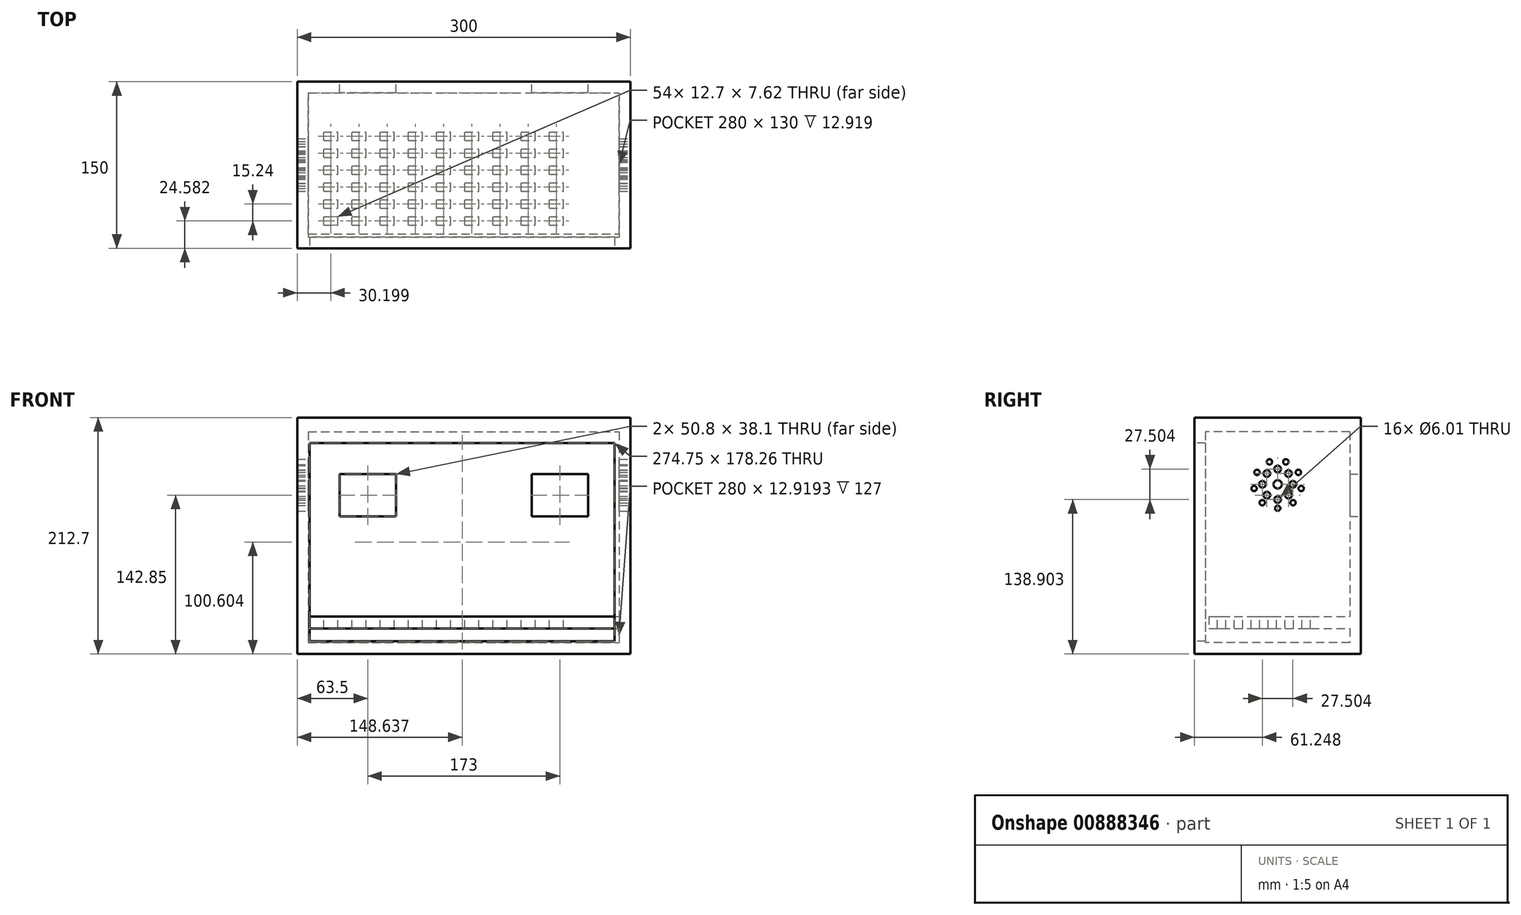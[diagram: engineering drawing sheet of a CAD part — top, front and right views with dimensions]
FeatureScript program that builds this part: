
annotation { "Feature Type Name" : "Feature", "Feature Type Description" : "" }
export const myFeature = defineFeature(function(context is Context, id is Id, definition is map)
    precondition{}
    {
        {
            var Q0;
            Q0=qCreatedBy(makeId("Top.planeOp"),FACE);
            var sketch = newSketch(context, id + "F0", { "sketchPlane" : qUnion([Q0])});
            skLineSegment(sketch, "E0.bottom", {"start": v(-150, 75) * mm, "end": v(150, 75) * mm});
            skLineSegment(sketch, "E0.top", {"start": v(-150, -75) * mm, "end": v(150, -75) * mm});
            skLineSegment(sketch, "E0.left", {"start": v(-150, 75) * mm, "end": v(-150, -75) * mm});
            skLineSegment(sketch, "E0.right", {"start": v(150, 75) * mm, "end": v(150, -75) * mm});
            skSolve(sketch);
        }
        {
            var Q0;
            Q0 = qSketchRegion(id + "F0", true);
            extrude(context, id + "F1", {"entities" : qUnion([Q0]), "depth" : 200 * mm, "offsetDistance" : 25.4 * mm});
        }
        {
            var Q0;
            Q0=makeQuery(id+"F1.opExtrude","CAP_FACE",FACE,{"disambiguationData":[OSD([sQuery(id+"F0.wireOp",EDGE,"E0.bottom"),sQuery(id+"F0.wireOp",EDGE,"E0.top"),sQuery(id+"F0.wireOp",EDGE,"E0.left"),sQuery(id+"F0.wireOp",EDGE,"E0.right")])],"isStart":false});
            shell(context, id + "F2", {"entities" : qUnion([Q0]), "thickness" : 10 * mm});
        }
        {
            var Q0;
            Q0=makeQuery(id+"F1.opExtrude","SWEPT_FACE",FACE,{"disambiguationData":[OSD([sQuery(id+"F0.wireOp",EDGE,"E0.top")])]});
            var sketch = newSketch(context, id + "F3", { "sketchPlane" : qUnion([Q0])});
            skLineSegment(sketch, "E1.bottom", {"start": v(-138.74, 11.48) * mm, "end": v(136.01, 11.48) * mm});
            skLineSegment(sketch, "E1.top", {"start": v(-138.74, 189.73) * mm, "end": v(136.01, 189.73) * mm});
            skLineSegment(sketch, "E1.left", {"start": v(-138.74, 11.48) * mm, "end": v(-138.74, 189.73) * mm});
            skLineSegment(sketch, "E1.right", {"start": v(136.01, 11.48) * mm, "end": v(136.01, 189.73) * mm});
            skSolve(sketch);
        }
        {
            var Q0;
            Q0=makeQuery(id+"F3.imprint","IMPRINT",FACE,{"disambiguationData":[TD([[makeQuery(id+"F3.imprint","IMPRINT",EDGE,{"derivedFrom":sQuery(id+"F3.wireOp",EDGE,"E1.bottom")}),1.0]])]});
            extrude(context, id + "F4", {"entities" : qUnion([Q0]), "operationType" : NewBodyOperationType.REMOVE, "oppositeDirection" : true, "depth" : 25.4 * mm, "offsetDistance" : 25.4 * mm});
        }
        {
            var Q0;
            Q0=makeQuery(id+"F1.opExtrude","SWEPT_FACE",FACE,{"disambiguationData":[OSD([sQuery(id+"F0.wireOp",EDGE,"E0.bottom")])]});
            var sketch = newSketch(context, id + "F5", { "sketchPlane" : qUnion([Q0])});
            skLineSegment(sketch, "E2.bottom", {"start": v(-111.9, 161.9) * mm, "end": v(-61.1, 161.9) * mm});
            skLineSegment(sketch, "E2.top", {"start": v(-111.9, 123.8) * mm, "end": v(-61.1, 123.8) * mm});
            skLineSegment(sketch, "E2.left", {"start": v(-111.9, 161.9) * mm, "end": v(-111.9, 123.8) * mm});
            skLineSegment(sketch, "E2.right", {"start": v(-61.1, 161.9) * mm, "end": v(-61.1, 123.8) * mm});
            skLineSegment(sketch, "E3.bottom", {"start": v(61.1, 161.9) * mm, "end": v(111.9, 161.9) * mm});
            skLineSegment(sketch, "E3.top", {"start": v(61.1, 123.8) * mm, "end": v(111.9, 123.8) * mm});
            skLineSegment(sketch, "E3.left", {"start": v(61.1, 161.9) * mm, "end": v(61.1, 123.8) * mm});
            skLineSegment(sketch, "E3.right", {"start": v(111.9, 161.9) * mm, "end": v(111.9, 123.8) * mm});
            skSolve(sketch);
        }
        {
            var Q0;
            Q0 = qSketchRegion(id + "F5", true);
            extrude(context, id + "F6", {"entities" : qUnion([Q0]), "operationType" : NewBodyOperationType.REMOVE, "oppositeDirection" : true, "depth" : 25.4 * mm, "offsetDistance" : 25.4 * mm});
        }
        {
            var Q0;
            Q0=makeQuery(id+"F1.opExtrude","SWEPT_FACE",FACE,{"disambiguationData":[OSD([sQuery(id+"F0.wireOp",EDGE,"E0.right")])]});
            var sketch = newSketch(context, id + "F7", { "sketchPlane" : qUnion([Q0])});
            skCircle(sketch, "E4", {"center": v(0, 152.65) * mm, "radius": 3.75 * mm});
            skCircle(sketch, "E5", {"center": v(0, 138.9) * mm, "radius": 3 * mm});
            skCircle(sketch, "E6.1.0", {"center": v(9.72, 142.93) * mm, "radius": 3 * mm});
            skCircle(sketch, "E6.2.0", {"center": v(13.75, 152.65) * mm, "radius": 3 * mm});
            skCircle(sketch, "E7.1.3.0", {"center": v(9.72, 162.38) * mm, "radius": 3 * mm});
            skCircle(sketch, "E7.1.4.0", {"center": v(0, 166.4) * mm, "radius": 3 * mm});
            skCircle(sketch, "E7.1.5.0", {"center": v(-9.72, 162.38) * mm, "radius": 3 * mm});
            skCircle(sketch, "E7.1.6.0", {"center": v(-13.75, 152.65) * mm, "radius": 3 * mm});
            skCircle(sketch, "E7.1.7.0", {"center": v(-9.72, 142.93) * mm, "radius": 3 * mm});
            skCircle(sketch, "E8", {"center": v(0, 131.1) * mm, "radius": 2.4 * mm});
            skPoint(sketch, "E8.centerSnap0", {"position": v(0, 0) * mm});
            skCircle(sketch, "E9.1.0", {"center": v(13.85, 136.15) * mm, "radius": 2.4 * mm});
            skCircle(sketch, "E9.2.0", {"center": v(21.22, 148.91) * mm, "radius": 2.4 * mm});
            skCircle(sketch, "E9.3.0", {"center": v(18.66, 163.43) * mm, "radius": 2.4 * mm});
            skCircle(sketch, "E9.4.0", {"center": v(7.37, 172.9) * mm, "radius": 2.4 * mm});
            skCircle(sketch, "E9.5.0", {"center": v(-7.37, 172.9) * mm, "radius": 2.4 * mm});
            skCircle(sketch, "E9.6.0", {"center": v(-18.66, 163.43) * mm, "radius": 2.4 * mm});
            skCircle(sketch, "E9.7.0", {"center": v(-21.22, 148.91) * mm, "radius": 2.4 * mm});
            skCircle(sketch, "E9.8.0", {"center": v(-13.85, 136.15) * mm, "radius": 2.4 * mm});
            skSolve(sketch);
        }
        {
            var Q0;
            Q0 = qSketchRegion(id + "F7", true);
            extrude(context, id + "F8", {"entities" : qUnion([Q0]), "operationType" : NewBodyOperationType.REMOVE, "endBound" : BoundingType.THROUGH_ALL, "oppositeDirection" : true, "depth" : 25.4 * mm, "offsetDistance" : 25.4 * mm});
        }
        {
            var Q0;
            Q0=makeQuery(id+"F1.opExtrude","CAP_FACE",FACE,{"disambiguationData":[OSD([sQuery(id+"F0.wireOp",EDGE,"E0.bottom"),sQuery(id+"F0.wireOp",EDGE,"E0.top"),sQuery(id+"F0.wireOp",EDGE,"E0.left"),sQuery(id+"F0.wireOp",EDGE,"E0.right")])],"isStart":false});
            var sketch = newSketch(context, id + "F9", { "sketchPlane" : qUnion([Q0])});
            skLineSegment(sketch, "E10.bottom", {"start": v(-150, 75) * mm, "end": v(150, 75) * mm});
            skLineSegment(sketch, "E10.top", {"start": v(-150, -75) * mm, "end": v(150, -75) * mm});
            skLineSegment(sketch, "E10.left", {"start": v(-150, 75) * mm, "end": v(-150, -75) * mm});
            skLineSegment(sketch, "E10.right", {"start": v(150, 75) * mm, "end": v(150, -75) * mm});
            skSolve(sketch);
        }
        {
            var Q0;
            Q0 = qSketchRegion(id + "F9", true);
            extrude(context, id + "F10", {"entities" : qUnion([Q0]), "operationType" : NewBodyOperationType.ADD, "depth" : 12.7 * mm, "offsetDistance" : 25.4 * mm});
        }
        {
            var Q0;
            Q0=makeQuery(id+"F2.opShell","OFFSET_FACE",FACE,{"disambiguationData":[OSD([sQuery(id+"F0.wireOp",EDGE,"E0.bottom")])]});
            var sketch = newSketch(context, id + "F11", { "sketchPlane" : qUnion([Q0])});
            skLineSegment(sketch, "E11.bottom", {"start": v(-140, 33.75) * mm, "end": v(140, 33.75) * mm});
            skLineSegment(sketch, "E11.top", {"start": v(-140, 22.92) * mm, "end": v(140, 22.92) * mm});
            skLineSegment(sketch, "E11.left", {"start": v(-140, 33.75) * mm, "end": v(-140, 22.92) * mm});
            skLineSegment(sketch, "E11.right", {"start": v(140, 33.75) * mm, "end": v(140, 22.92) * mm});
            skSolve(sketch);
        }
        {
            var Q0;
            Q0=makeQuery(id+"F11.imprint","IMPRINT",FACE,{"disambiguationData":[TD([[makeQuery(id+"F11.imprint","IMPRINT",EDGE,{"derivedFrom":sQuery(id+"F11.wireOp",EDGE,"E11.bottom")}),-1.0]])]});
            extrude(context, id + "F12", {"entities" : qUnion([Q0]), "operationType" : NewBodyOperationType.ADD, "depth" : 127 * mm, "offsetDistance" : 25.4 * mm});
        }
        {
            var Q0;
            Q0=makeQuery(id+"F12.opExtrude","SWEPT_FACE",FACE,{"disambiguationData":[OSD([sQuery(id+"F11.wireOp",EDGE,"E11.bottom")])]});
            var sketch = newSketch(context, id + "F13", { "sketchPlane" : qUnion([Q0])});
            skLineSegment(sketch, "E12.bottom", {"start": v(-126.15, -54.23) * mm, "end": v(-113.45, -54.23) * mm});
            skLineSegment(sketch, "E12.top", {"start": v(-126.15, -46.6) * mm, "end": v(-113.45, -46.6) * mm});
            skLineSegment(sketch, "E12.left", {"start": v(-126.15, -54.23) * mm, "end": v(-126.15, -46.6) * mm});
            skLineSegment(sketch, "E12.right", {"start": v(-113.45, -54.23) * mm, "end": v(-113.45, -46.6) * mm});
            skLineSegment(sketch, "E13.0.1.0", {"start": v(-126.15, -31.37) * mm, "end": v(-113.45, -31.37) * mm});
            skLineSegment(sketch, "E13.0.1.1", {"start": v(-126.15, -38.99) * mm, "end": v(-126.15, -31.37) * mm});
            skLineSegment(sketch, "E13.0.1.2", {"start": v(-126.15, -38.99) * mm, "end": v(-113.45, -38.99) * mm});
            skLineSegment(sketch, "E13.0.1.3", {"start": v(-113.45, -38.99) * mm, "end": v(-113.45, -31.37) * mm});
            skLineSegment(sketch, "E13.0.2.0", {"start": v(-126.15, -16.13) * mm, "end": v(-113.45, -16.13) * mm});
            skLineSegment(sketch, "E13.0.2.1", {"start": v(-126.15, -23.75) * mm, "end": v(-126.15, -16.13) * mm});
            skLineSegment(sketch, "E13.0.2.2", {"start": v(-126.15, -23.75) * mm, "end": v(-113.45, -23.75) * mm});
            skLineSegment(sketch, "E13.0.2.3", {"start": v(-113.45, -23.75) * mm, "end": v(-113.45, -16.13) * mm});
            skLineSegment(sketch, "E13.0.3.0", {"start": v(-126.15, -0.89) * mm, "end": v(-113.45, -0.89) * mm});
            skLineSegment(sketch, "E13.0.3.1", {"start": v(-126.15, -8.5) * mm, "end": v(-126.15, -0.89) * mm});
            skLineSegment(sketch, "E13.0.3.2", {"start": v(-126.15, -8.5) * mm, "end": v(-113.45, -8.5) * mm});
            skLineSegment(sketch, "E13.0.3.3", {"start": v(-113.45, -8.5) * mm, "end": v(-113.45, -0.89) * mm});
            skLineSegment(sketch, "E13.0.4.0", {"start": v(-126.15, 14.35) * mm, "end": v(-113.45, 14.35) * mm});
            skLineSegment(sketch, "E13.0.4.1", {"start": v(-126.15, 6.73) * mm, "end": v(-126.15, 14.35) * mm});
            skLineSegment(sketch, "E13.0.4.2", {"start": v(-126.15, 6.73) * mm, "end": v(-113.45, 6.73) * mm});
            skLineSegment(sketch, "E13.0.4.3", {"start": v(-113.45, 6.73) * mm, "end": v(-113.45, 14.35) * mm});
            skLineSegment(sketch, "E13.0.5.0", {"start": v(-126.15, 29.6) * mm, "end": v(-113.45, 29.6) * mm});
            skLineSegment(sketch, "E13.0.5.1", {"start": v(-126.15, 21.97) * mm, "end": v(-126.15, 29.6) * mm});
            skLineSegment(sketch, "E13.0.5.2", {"start": v(-126.15, 21.97) * mm, "end": v(-113.45, 21.97) * mm});
            skLineSegment(sketch, "E13.0.5.3", {"start": v(-113.45, 21.97) * mm, "end": v(-113.45, 29.6) * mm});
            skLineSegment(sketch, "E13.1.0.0", {"start": v(-100.75, -46.6) * mm, "end": v(-88.05, -46.6) * mm});
            skLineSegment(sketch, "E13.1.0.1", {"start": v(-100.75, -54.23) * mm, "end": v(-100.75, -46.6) * mm});
            skLineSegment(sketch, "E13.1.0.2", {"start": v(-100.75, -54.23) * mm, "end": v(-88.05, -54.23) * mm});
            skLineSegment(sketch, "E13.1.0.3", {"start": v(-88.05, -54.23) * mm, "end": v(-88.05, -46.6) * mm});
            skLineSegment(sketch, "E13.1.1.0", {"start": v(-100.75, -31.37) * mm, "end": v(-88.05, -31.37) * mm});
            skLineSegment(sketch, "E13.1.1.1", {"start": v(-100.75, -38.99) * mm, "end": v(-100.75, -31.37) * mm});
            skLineSegment(sketch, "E13.1.1.2", {"start": v(-100.75, -38.99) * mm, "end": v(-88.05, -38.99) * mm});
            skLineSegment(sketch, "E13.1.1.3", {"start": v(-88.05, -38.99) * mm, "end": v(-88.05, -31.37) * mm});
            skLineSegment(sketch, "E13.1.2.0", {"start": v(-100.75, -16.13) * mm, "end": v(-88.05, -16.13) * mm});
            skLineSegment(sketch, "E13.1.2.1", {"start": v(-100.75, -23.75) * mm, "end": v(-100.75, -16.13) * mm});
            skLineSegment(sketch, "E13.1.2.2", {"start": v(-100.75, -23.75) * mm, "end": v(-88.05, -23.75) * mm});
            skLineSegment(sketch, "E13.1.2.3", {"start": v(-88.05, -23.75) * mm, "end": v(-88.05, -16.13) * mm});
            skLineSegment(sketch, "E13.1.3.0", {"start": v(-100.75, -0.89) * mm, "end": v(-88.05, -0.89) * mm});
            skLineSegment(sketch, "E13.1.3.1", {"start": v(-100.75, -8.5) * mm, "end": v(-100.75, -0.89) * mm});
            skLineSegment(sketch, "E13.1.3.2", {"start": v(-100.75, -8.5) * mm, "end": v(-88.05, -8.5) * mm});
            skLineSegment(sketch, "E13.1.3.3", {"start": v(-88.05, -8.5) * mm, "end": v(-88.05, -0.89) * mm});
            skLineSegment(sketch, "E13.1.4.0", {"start": v(-100.75, 14.35) * mm, "end": v(-88.05, 14.35) * mm});
            skLineSegment(sketch, "E13.1.4.1", {"start": v(-100.75, 6.73) * mm, "end": v(-100.75, 14.35) * mm});
            skLineSegment(sketch, "E13.1.4.2", {"start": v(-100.75, 6.73) * mm, "end": v(-88.05, 6.73) * mm});
            skLineSegment(sketch, "E13.1.4.3", {"start": v(-88.05, 6.73) * mm, "end": v(-88.05, 14.35) * mm});
            skLineSegment(sketch, "E13.1.5.0", {"start": v(-100.75, 29.6) * mm, "end": v(-88.05, 29.6) * mm});
            skLineSegment(sketch, "E13.1.5.1", {"start": v(-100.75, 21.97) * mm, "end": v(-100.75, 29.6) * mm});
            skLineSegment(sketch, "E13.1.5.2", {"start": v(-100.75, 21.97) * mm, "end": v(-88.05, 21.97) * mm});
            skLineSegment(sketch, "E13.1.5.3", {"start": v(-88.05, 21.97) * mm, "end": v(-88.05, 29.6) * mm});
            skLineSegment(sketch, "E13.2.0.0", {"start": v(-75.35, -46.6) * mm, "end": v(-62.65, -46.6) * mm});
            skLineSegment(sketch, "E13.2.0.1", {"start": v(-75.35, -54.23) * mm, "end": v(-75.35, -46.6) * mm});
            skLineSegment(sketch, "E13.2.0.2", {"start": v(-75.35, -54.23) * mm, "end": v(-62.65, -54.23) * mm});
            skLineSegment(sketch, "E13.2.0.3", {"start": v(-62.65, -54.23) * mm, "end": v(-62.65, -46.6) * mm});
            skLineSegment(sketch, "E13.2.1.0", {"start": v(-75.35, -31.37) * mm, "end": v(-62.65, -31.37) * mm});
            skLineSegment(sketch, "E13.2.1.1", {"start": v(-75.35, -38.99) * mm, "end": v(-75.35, -31.37) * mm});
            skLineSegment(sketch, "E13.2.1.2", {"start": v(-75.35, -38.99) * mm, "end": v(-62.65, -38.99) * mm});
            skLineSegment(sketch, "E13.2.1.3", {"start": v(-62.65, -38.99) * mm, "end": v(-62.65, -31.37) * mm});
            skLineSegment(sketch, "E13.2.2.0", {"start": v(-75.35, -16.13) * mm, "end": v(-62.65, -16.13) * mm});
            skLineSegment(sketch, "E13.2.2.1", {"start": v(-75.35, -23.75) * mm, "end": v(-75.35, -16.13) * mm});
            skLineSegment(sketch, "E13.2.2.2", {"start": v(-75.35, -23.75) * mm, "end": v(-62.65, -23.75) * mm});
            skLineSegment(sketch, "E13.2.2.3", {"start": v(-62.65, -23.75) * mm, "end": v(-62.65, -16.13) * mm});
            skLineSegment(sketch, "E13.2.3.0", {"start": v(-75.35, -0.89) * mm, "end": v(-62.65, -0.89) * mm});
            skLineSegment(sketch, "E13.2.3.1", {"start": v(-75.35, -8.5) * mm, "end": v(-75.35, -0.89) * mm});
            skLineSegment(sketch, "E13.2.3.2", {"start": v(-75.35, -8.5) * mm, "end": v(-62.65, -8.5) * mm});
            skLineSegment(sketch, "E13.2.3.3", {"start": v(-62.65, -8.5) * mm, "end": v(-62.65, -0.89) * mm});
            skLineSegment(sketch, "E13.2.4.0", {"start": v(-75.35, 14.35) * mm, "end": v(-62.65, 14.35) * mm});
            skLineSegment(sketch, "E13.2.4.1", {"start": v(-75.35, 6.73) * mm, "end": v(-75.35, 14.35) * mm});
            skLineSegment(sketch, "E13.2.4.2", {"start": v(-75.35, 6.73) * mm, "end": v(-62.65, 6.73) * mm});
            skLineSegment(sketch, "E13.2.4.3", {"start": v(-62.65, 6.73) * mm, "end": v(-62.65, 14.35) * mm});
            skLineSegment(sketch, "E13.2.5.0", {"start": v(-75.35, 29.6) * mm, "end": v(-62.65, 29.6) * mm});
            skLineSegment(sketch, "E13.2.5.1", {"start": v(-75.35, 21.97) * mm, "end": v(-75.35, 29.6) * mm});
            skLineSegment(sketch, "E13.2.5.2", {"start": v(-75.35, 21.97) * mm, "end": v(-62.65, 21.97) * mm});
            skLineSegment(sketch, "E13.2.5.3", {"start": v(-62.65, 21.97) * mm, "end": v(-62.65, 29.6) * mm});
            skLineSegment(sketch, "E13.3.0.0", {"start": v(-49.95, -46.6) * mm, "end": v(-37.25, -46.6) * mm});
            skLineSegment(sketch, "E13.3.0.1", {"start": v(-49.95, -54.23) * mm, "end": v(-49.95, -46.6) * mm});
            skLineSegment(sketch, "E13.3.0.2", {"start": v(-49.95, -54.23) * mm, "end": v(-37.25, -54.23) * mm});
            skLineSegment(sketch, "E13.3.0.3", {"start": v(-37.25, -54.23) * mm, "end": v(-37.25, -46.6) * mm});
            skLineSegment(sketch, "E13.3.1.0", {"start": v(-49.95, -31.37) * mm, "end": v(-37.25, -31.37) * mm});
            skLineSegment(sketch, "E13.3.1.1", {"start": v(-49.95, -38.99) * mm, "end": v(-49.95, -31.37) * mm});
            skLineSegment(sketch, "E13.3.1.2", {"start": v(-49.95, -38.99) * mm, "end": v(-37.25, -38.99) * mm});
            skLineSegment(sketch, "E13.3.1.3", {"start": v(-37.25, -38.99) * mm, "end": v(-37.25, -31.37) * mm});
            skLineSegment(sketch, "E13.3.2.0", {"start": v(-49.95, -16.13) * mm, "end": v(-37.25, -16.13) * mm});
            skLineSegment(sketch, "E13.3.2.1", {"start": v(-49.95, -23.75) * mm, "end": v(-49.95, -16.13) * mm});
            skLineSegment(sketch, "E13.3.2.2", {"start": v(-49.95, -23.75) * mm, "end": v(-37.25, -23.75) * mm});
            skLineSegment(sketch, "E13.3.2.3", {"start": v(-37.25, -23.75) * mm, "end": v(-37.25, -16.13) * mm});
            skLineSegment(sketch, "E13.3.3.0", {"start": v(-49.95, -0.89) * mm, "end": v(-37.25, -0.89) * mm});
            skLineSegment(sketch, "E13.3.3.1", {"start": v(-49.95, -8.5) * mm, "end": v(-49.95, -0.89) * mm});
            skLineSegment(sketch, "E13.3.3.2", {"start": v(-49.95, -8.5) * mm, "end": v(-37.25, -8.5) * mm});
            skLineSegment(sketch, "E13.3.3.3", {"start": v(-37.25, -8.5) * mm, "end": v(-37.25, -0.89) * mm});
            skLineSegment(sketch, "E13.3.4.0", {"start": v(-49.95, 14.35) * mm, "end": v(-37.25, 14.35) * mm});
            skLineSegment(sketch, "E13.3.4.1", {"start": v(-49.95, 6.73) * mm, "end": v(-49.95, 14.35) * mm});
            skLineSegment(sketch, "E13.3.4.2", {"start": v(-49.95, 6.73) * mm, "end": v(-37.25, 6.73) * mm});
            skLineSegment(sketch, "E13.3.4.3", {"start": v(-37.25, 6.73) * mm, "end": v(-37.25, 14.35) * mm});
            skLineSegment(sketch, "E13.3.5.0", {"start": v(-49.95, 29.6) * mm, "end": v(-37.25, 29.6) * mm});
            skLineSegment(sketch, "E13.3.5.1", {"start": v(-49.95, 21.97) * mm, "end": v(-49.95, 29.6) * mm});
            skLineSegment(sketch, "E13.3.5.2", {"start": v(-49.95, 21.97) * mm, "end": v(-37.25, 21.97) * mm});
            skLineSegment(sketch, "E13.3.5.3", {"start": v(-37.25, 21.97) * mm, "end": v(-37.25, 29.6) * mm});
            skLineSegment(sketch, "E13.4.0.0", {"start": v(-24.55, -46.6) * mm, "end": v(-11.85, -46.6) * mm});
            skLineSegment(sketch, "E13.4.0.1", {"start": v(-24.55, -54.23) * mm, "end": v(-24.55, -46.6) * mm});
            skLineSegment(sketch, "E13.4.0.2", {"start": v(-24.55, -54.23) * mm, "end": v(-11.85, -54.23) * mm});
            skLineSegment(sketch, "E13.4.0.3", {"start": v(-11.85, -54.23) * mm, "end": v(-11.85, -46.6) * mm});
            skLineSegment(sketch, "E13.4.1.0", {"start": v(-24.55, -31.37) * mm, "end": v(-11.85, -31.37) * mm});
            skLineSegment(sketch, "E13.4.1.1", {"start": v(-24.55, -38.99) * mm, "end": v(-24.55, -31.37) * mm});
            skLineSegment(sketch, "E13.4.1.2", {"start": v(-24.55, -38.99) * mm, "end": v(-11.85, -38.99) * mm});
            skLineSegment(sketch, "E13.4.1.3", {"start": v(-11.85, -38.99) * mm, "end": v(-11.85, -31.37) * mm});
            skLineSegment(sketch, "E13.4.2.0", {"start": v(-24.55, -16.13) * mm, "end": v(-11.85, -16.13) * mm});
            skLineSegment(sketch, "E13.4.2.1", {"start": v(-24.55, -23.75) * mm, "end": v(-24.55, -16.13) * mm});
            skLineSegment(sketch, "E13.4.2.2", {"start": v(-24.55, -23.75) * mm, "end": v(-11.85, -23.75) * mm});
            skLineSegment(sketch, "E13.4.2.3", {"start": v(-11.85, -23.75) * mm, "end": v(-11.85, -16.13) * mm});
            skLineSegment(sketch, "E13.4.3.0", {"start": v(-24.55, -0.89) * mm, "end": v(-11.85, -0.89) * mm});
            skLineSegment(sketch, "E13.4.3.1", {"start": v(-24.55, -8.5) * mm, "end": v(-24.55, -0.89) * mm});
            skLineSegment(sketch, "E13.4.3.2", {"start": v(-24.55, -8.5) * mm, "end": v(-11.85, -8.5) * mm});
            skLineSegment(sketch, "E13.4.3.3", {"start": v(-11.85, -8.5) * mm, "end": v(-11.85, -0.89) * mm});
            skLineSegment(sketch, "E13.4.4.0", {"start": v(-24.55, 14.35) * mm, "end": v(-11.85, 14.35) * mm});
            skLineSegment(sketch, "E13.4.4.1", {"start": v(-24.55, 6.73) * mm, "end": v(-24.55, 14.35) * mm});
            skLineSegment(sketch, "E13.4.4.2", {"start": v(-24.55, 6.73) * mm, "end": v(-11.85, 6.73) * mm});
            skLineSegment(sketch, "E13.4.4.3", {"start": v(-11.85, 6.73) * mm, "end": v(-11.85, 14.35) * mm});
            skLineSegment(sketch, "E13.4.5.0", {"start": v(-24.55, 29.6) * mm, "end": v(-11.85, 29.6) * mm});
            skLineSegment(sketch, "E13.4.5.1", {"start": v(-24.55, 21.97) * mm, "end": v(-24.55, 29.6) * mm});
            skLineSegment(sketch, "E13.4.5.2", {"start": v(-24.55, 21.97) * mm, "end": v(-11.85, 21.97) * mm});
            skLineSegment(sketch, "E13.4.5.3", {"start": v(-11.85, 21.97) * mm, "end": v(-11.85, 29.6) * mm});
            skLineSegment(sketch, "E13.5.0.0", {"start": v(0.85, -46.6) * mm, "end": v(13.55, -46.6) * mm});
            skLineSegment(sketch, "E13.5.0.1", {"start": v(0.85, -54.23) * mm, "end": v(0.85, -46.6) * mm});
            skLineSegment(sketch, "E13.5.0.2", {"start": v(0.85, -54.23) * mm, "end": v(13.55, -54.23) * mm});
            skLineSegment(sketch, "E13.5.0.3", {"start": v(13.55, -54.23) * mm, "end": v(13.55, -46.6) * mm});
            skLineSegment(sketch, "E13.5.1.0", {"start": v(0.85, -31.37) * mm, "end": v(13.55, -31.37) * mm});
            skLineSegment(sketch, "E13.5.1.1", {"start": v(0.85, -38.99) * mm, "end": v(0.85, -31.37) * mm});
            skLineSegment(sketch, "E13.5.1.2", {"start": v(0.85, -38.99) * mm, "end": v(13.55, -38.99) * mm});
            skLineSegment(sketch, "E13.5.1.3", {"start": v(13.55, -38.99) * mm, "end": v(13.55, -31.37) * mm});
            skLineSegment(sketch, "E13.5.2.0", {"start": v(0.85, -16.13) * mm, "end": v(13.55, -16.13) * mm});
            skLineSegment(sketch, "E13.5.2.1", {"start": v(0.85, -23.75) * mm, "end": v(0.85, -16.13) * mm});
            skLineSegment(sketch, "E13.5.2.2", {"start": v(0.85, -23.75) * mm, "end": v(13.55, -23.75) * mm});
            skLineSegment(sketch, "E13.5.2.3", {"start": v(13.55, -23.75) * mm, "end": v(13.55, -16.13) * mm});
            skLineSegment(sketch, "E13.5.3.0", {"start": v(0.85, -0.89) * mm, "end": v(13.55, -0.89) * mm});
            skLineSegment(sketch, "E13.5.3.1", {"start": v(0.85, -8.5) * mm, "end": v(0.85, -0.89) * mm});
            skLineSegment(sketch, "E13.5.3.2", {"start": v(0.85, -8.5) * mm, "end": v(13.55, -8.5) * mm});
            skLineSegment(sketch, "E13.5.3.3", {"start": v(13.55, -8.5) * mm, "end": v(13.55, -0.89) * mm});
            skLineSegment(sketch, "E13.5.4.0", {"start": v(0.85, 14.35) * mm, "end": v(13.55, 14.35) * mm});
            skLineSegment(sketch, "E13.5.4.1", {"start": v(0.85, 6.73) * mm, "end": v(0.85, 14.35) * mm});
            skLineSegment(sketch, "E13.5.4.2", {"start": v(0.85, 6.73) * mm, "end": v(13.55, 6.73) * mm});
            skLineSegment(sketch, "E13.5.4.3", {"start": v(13.55, 6.73) * mm, "end": v(13.55, 14.35) * mm});
            skLineSegment(sketch, "E13.5.5.0", {"start": v(0.85, 29.6) * mm, "end": v(13.55, 29.6) * mm});
            skLineSegment(sketch, "E13.5.5.1", {"start": v(0.85, 21.97) * mm, "end": v(0.85, 29.6) * mm});
            skLineSegment(sketch, "E13.5.5.2", {"start": v(0.85, 21.97) * mm, "end": v(13.55, 21.97) * mm});
            skLineSegment(sketch, "E13.5.5.3", {"start": v(13.55, 21.97) * mm, "end": v(13.55, 29.6) * mm});
            skLineSegment(sketch, "E13.6.0.0", {"start": v(26.25, -46.6) * mm, "end": v(38.95, -46.6) * mm});
            skLineSegment(sketch, "E13.6.0.1", {"start": v(26.25, -54.23) * mm, "end": v(26.25, -46.6) * mm});
            skLineSegment(sketch, "E13.6.0.2", {"start": v(26.25, -54.23) * mm, "end": v(38.95, -54.23) * mm});
            skLineSegment(sketch, "E13.6.0.3", {"start": v(38.95, -54.23) * mm, "end": v(38.95, -46.6) * mm});
            skLineSegment(sketch, "E13.6.1.0", {"start": v(26.25, -31.37) * mm, "end": v(38.95, -31.37) * mm});
            skLineSegment(sketch, "E13.6.1.1", {"start": v(26.25, -38.99) * mm, "end": v(26.25, -31.37) * mm});
            skLineSegment(sketch, "E13.6.1.2", {"start": v(26.25, -38.99) * mm, "end": v(38.95, -38.99) * mm});
            skLineSegment(sketch, "E13.6.1.3", {"start": v(38.95, -38.99) * mm, "end": v(38.95, -31.37) * mm});
            skLineSegment(sketch, "E13.6.2.0", {"start": v(26.25, -16.13) * mm, "end": v(38.95, -16.13) * mm});
            skLineSegment(sketch, "E13.6.2.1", {"start": v(26.25, -23.75) * mm, "end": v(26.25, -16.13) * mm});
            skLineSegment(sketch, "E13.6.2.2", {"start": v(26.25, -23.75) * mm, "end": v(38.95, -23.75) * mm});
            skLineSegment(sketch, "E13.6.2.3", {"start": v(38.95, -23.75) * mm, "end": v(38.95, -16.13) * mm});
            skLineSegment(sketch, "E13.6.3.0", {"start": v(26.25, -0.89) * mm, "end": v(38.95, -0.89) * mm});
            skLineSegment(sketch, "E13.6.3.1", {"start": v(26.25, -8.5) * mm, "end": v(26.25, -0.89) * mm});
            skLineSegment(sketch, "E13.6.3.2", {"start": v(26.25, -8.5) * mm, "end": v(38.95, -8.5) * mm});
            skLineSegment(sketch, "E13.6.3.3", {"start": v(38.95, -8.5) * mm, "end": v(38.95, -0.89) * mm});
            skLineSegment(sketch, "E13.6.4.0", {"start": v(26.25, 14.35) * mm, "end": v(38.95, 14.35) * mm});
            skLineSegment(sketch, "E13.6.4.1", {"start": v(26.25, 6.73) * mm, "end": v(26.25, 14.35) * mm});
            skLineSegment(sketch, "E13.6.4.2", {"start": v(26.25, 6.73) * mm, "end": v(38.95, 6.73) * mm});
            skLineSegment(sketch, "E13.6.4.3", {"start": v(38.95, 6.73) * mm, "end": v(38.95, 14.35) * mm});
            skLineSegment(sketch, "E13.6.5.0", {"start": v(26.25, 29.6) * mm, "end": v(38.95, 29.6) * mm});
            skLineSegment(sketch, "E13.6.5.1", {"start": v(26.25, 21.97) * mm, "end": v(26.25, 29.6) * mm});
            skLineSegment(sketch, "E13.6.5.2", {"start": v(26.25, 21.97) * mm, "end": v(38.95, 21.97) * mm});
            skLineSegment(sketch, "E13.6.5.3", {"start": v(38.95, 21.97) * mm, "end": v(38.95, 29.6) * mm});
            skLineSegment(sketch, "E13.7.0.0", {"start": v(51.65, -46.6) * mm, "end": v(64.35, -46.6) * mm});
            skLineSegment(sketch, "E13.7.0.1", {"start": v(51.65, -54.23) * mm, "end": v(51.65, -46.6) * mm});
            skLineSegment(sketch, "E13.7.0.2", {"start": v(51.65, -54.23) * mm, "end": v(64.35, -54.23) * mm});
            skLineSegment(sketch, "E13.7.0.3", {"start": v(64.35, -54.23) * mm, "end": v(64.35, -46.6) * mm});
            skLineSegment(sketch, "E13.7.1.0", {"start": v(51.65, -31.37) * mm, "end": v(64.35, -31.37) * mm});
            skLineSegment(sketch, "E13.7.1.1", {"start": v(51.65, -38.99) * mm, "end": v(51.65, -31.37) * mm});
            skLineSegment(sketch, "E13.7.1.2", {"start": v(51.65, -38.99) * mm, "end": v(64.35, -38.99) * mm});
            skLineSegment(sketch, "E13.7.1.3", {"start": v(64.35, -38.99) * mm, "end": v(64.35, -31.37) * mm});
            skLineSegment(sketch, "E13.7.2.0", {"start": v(51.65, -16.13) * mm, "end": v(64.35, -16.13) * mm});
            skLineSegment(sketch, "E13.7.2.1", {"start": v(51.65, -23.75) * mm, "end": v(51.65, -16.13) * mm});
            skLineSegment(sketch, "E13.7.2.2", {"start": v(51.65, -23.75) * mm, "end": v(64.35, -23.75) * mm});
            skLineSegment(sketch, "E13.7.2.3", {"start": v(64.35, -23.75) * mm, "end": v(64.35, -16.13) * mm});
            skLineSegment(sketch, "E13.7.3.0", {"start": v(51.65, -0.89) * mm, "end": v(64.35, -0.89) * mm});
            skLineSegment(sketch, "E13.7.3.1", {"start": v(51.65, -8.5) * mm, "end": v(51.65, -0.89) * mm});
            skLineSegment(sketch, "E13.7.3.2", {"start": v(51.65, -8.5) * mm, "end": v(64.35, -8.5) * mm});
            skLineSegment(sketch, "E13.7.3.3", {"start": v(64.35, -8.5) * mm, "end": v(64.35, -0.89) * mm});
            skLineSegment(sketch, "E13.7.4.0", {"start": v(51.65, 14.35) * mm, "end": v(64.35, 14.35) * mm});
            skLineSegment(sketch, "E13.7.4.1", {"start": v(51.65, 6.73) * mm, "end": v(51.65, 14.35) * mm});
            skLineSegment(sketch, "E13.7.4.2", {"start": v(51.65, 6.73) * mm, "end": v(64.35, 6.73) * mm});
            skLineSegment(sketch, "E13.7.4.3", {"start": v(64.35, 6.73) * mm, "end": v(64.35, 14.35) * mm});
            skLineSegment(sketch, "E13.7.5.0", {"start": v(51.65, 29.6) * mm, "end": v(64.35, 29.6) * mm});
            skLineSegment(sketch, "E13.7.5.1", {"start": v(51.65, 21.97) * mm, "end": v(51.65, 29.6) * mm});
            skLineSegment(sketch, "E13.7.5.2", {"start": v(51.65, 21.97) * mm, "end": v(64.35, 21.97) * mm});
            skLineSegment(sketch, "E13.7.5.3", {"start": v(64.35, 21.97) * mm, "end": v(64.35, 29.6) * mm});
            skLineSegment(sketch, "E13.8.0.0", {"start": v(77.05, -46.6) * mm, "end": v(89.75, -46.6) * mm});
            skLineSegment(sketch, "E13.8.0.1", {"start": v(77.05, -54.23) * mm, "end": v(77.05, -46.6) * mm});
            skLineSegment(sketch, "E13.8.0.2", {"start": v(77.05, -54.23) * mm, "end": v(89.75, -54.23) * mm});
            skLineSegment(sketch, "E13.8.0.3", {"start": v(89.75, -54.23) * mm, "end": v(89.75, -46.6) * mm});
            skLineSegment(sketch, "E13.8.1.0", {"start": v(77.05, -31.37) * mm, "end": v(89.75, -31.37) * mm});
            skLineSegment(sketch, "E13.8.1.1", {"start": v(77.05, -38.99) * mm, "end": v(77.05, -31.37) * mm});
            skLineSegment(sketch, "E13.8.1.2", {"start": v(77.05, -38.99) * mm, "end": v(89.75, -38.99) * mm});
            skLineSegment(sketch, "E13.8.1.3", {"start": v(89.75, -38.99) * mm, "end": v(89.75, -31.37) * mm});
            skLineSegment(sketch, "E13.8.2.0", {"start": v(77.05, -16.13) * mm, "end": v(89.75, -16.13) * mm});
            skLineSegment(sketch, "E13.8.2.1", {"start": v(77.05, -23.75) * mm, "end": v(77.05, -16.13) * mm});
            skLineSegment(sketch, "E13.8.2.2", {"start": v(77.05, -23.75) * mm, "end": v(89.75, -23.75) * mm});
            skLineSegment(sketch, "E13.8.2.3", {"start": v(89.75, -23.75) * mm, "end": v(89.75, -16.13) * mm});
            skLineSegment(sketch, "E13.8.3.0", {"start": v(77.05, -0.89) * mm, "end": v(89.75, -0.89) * mm});
            skLineSegment(sketch, "E13.8.3.1", {"start": v(77.05, -8.5) * mm, "end": v(77.05, -0.89) * mm});
            skLineSegment(sketch, "E13.8.3.2", {"start": v(77.05, -8.5) * mm, "end": v(89.75, -8.5) * mm});
            skLineSegment(sketch, "E13.8.3.3", {"start": v(89.75, -8.5) * mm, "end": v(89.75, -0.89) * mm});
            skLineSegment(sketch, "E13.8.4.0", {"start": v(77.05, 14.35) * mm, "end": v(89.75, 14.35) * mm});
            skLineSegment(sketch, "E13.8.4.1", {"start": v(77.05, 6.73) * mm, "end": v(77.05, 14.35) * mm});
            skLineSegment(sketch, "E13.8.4.2", {"start": v(77.05, 6.73) * mm, "end": v(89.75, 6.73) * mm});
            skLineSegment(sketch, "E13.8.4.3", {"start": v(89.75, 6.73) * mm, "end": v(89.75, 14.35) * mm});
            skLineSegment(sketch, "E13.8.5.0", {"start": v(77.05, 29.6) * mm, "end": v(89.75, 29.6) * mm});
            skLineSegment(sketch, "E13.8.5.1", {"start": v(77.05, 21.97) * mm, "end": v(77.05, 29.6) * mm});
            skLineSegment(sketch, "E13.8.5.2", {"start": v(77.05, 21.97) * mm, "end": v(89.75, 21.97) * mm});
            skLineSegment(sketch, "E13.8.5.3", {"start": v(89.75, 21.97) * mm, "end": v(89.75, 29.6) * mm});
            skLineSegment(sketch, "E13.direction1", {"start": v(-126.15, -46.6) * mm, "end": v(-100.75, -46.6) * mm, "construction": true});
            skLineSegment(sketch, "E13.direction2", {"start": v(-126.15, -46.6) * mm, "end": v(-126.15, -31.37) * mm, "construction": true});
            skSolve(sketch);
        }
        {
            var Q0;
            Q0 = qSketchRegion(id + "F13", true);
            extrude(context, id + "F14", {"entities" : qUnion([Q0]), "operationType" : NewBodyOperationType.REMOVE, "oppositeDirection" : true, "depth" : 12.7 * mm, "offsetDistance" : 25.4 * mm});
        }
    });
